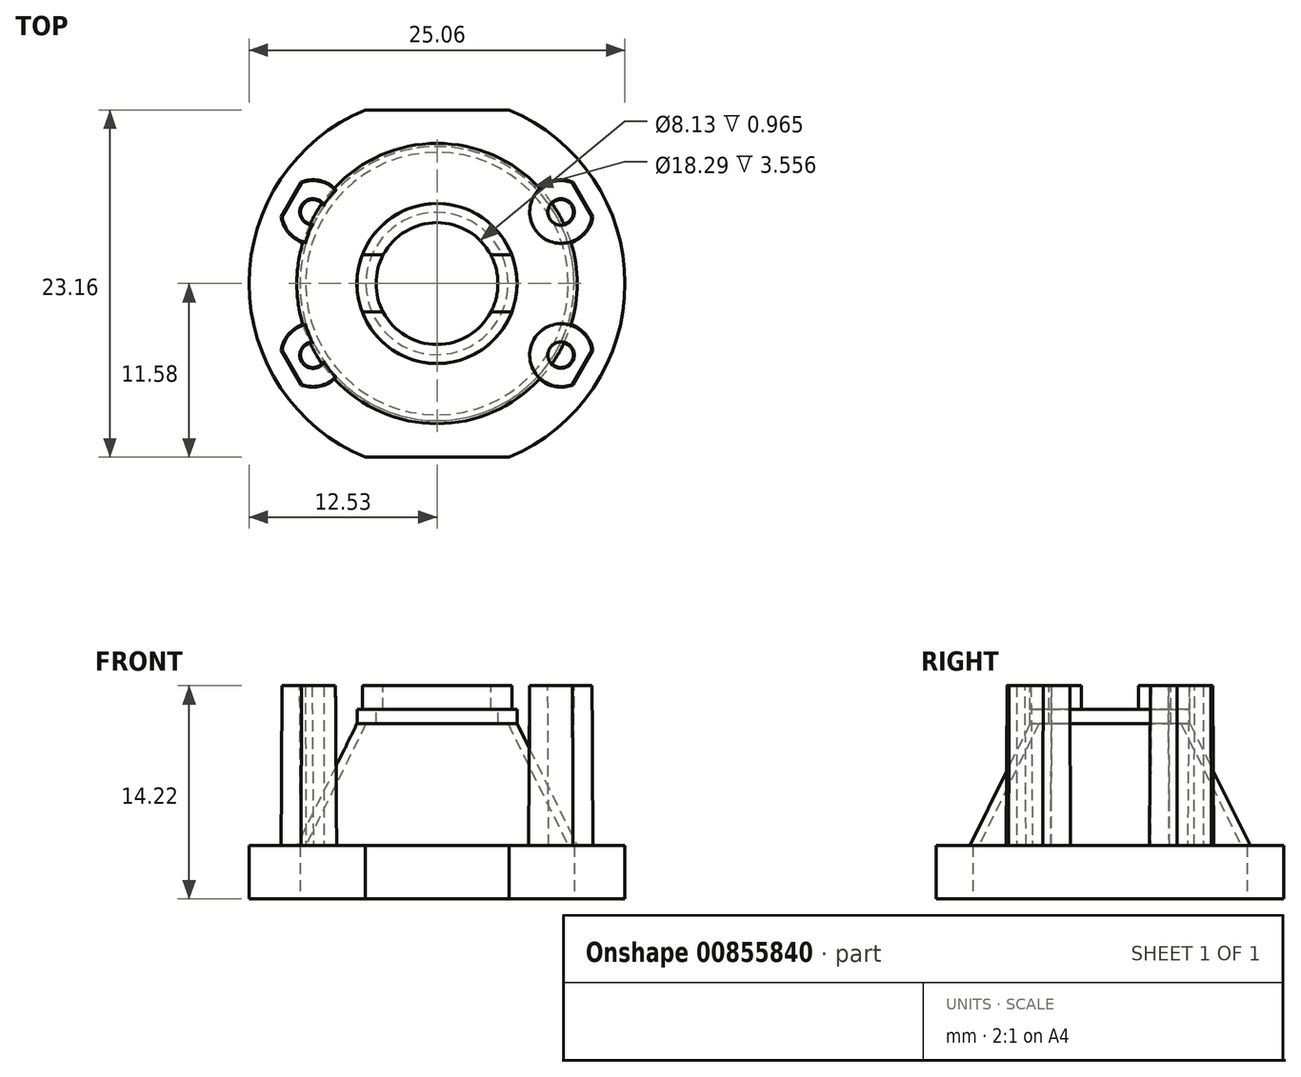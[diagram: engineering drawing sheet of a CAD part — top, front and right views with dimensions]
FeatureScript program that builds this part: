
annotation { "Feature Type Name" : "Feature", "Feature Type Description" : "" }
export const myFeature = defineFeature(function(context is Context, id is Id, definition is map)
    precondition{}
    {
        {
            var Q0;
            Q0=qCreatedBy(makeId("Top.planeOp"),FACE);
            var sketch = newSketch(context, id + "F0", { "sketchPlane" : qUnion([Q0])});
            skArc(sketch, "E0", {"start": v(-4.8, 11.58) * mm, "mid": v(-12.53, 0) * mm, "end": v(-4.8, -11.58) * mm});
            skCircle(sketch, "E1", {"center": v(0, 0) * mm, "radius": 9.14 * mm});
            skLineSegment(sketch, "E2", {"start": v(-4.8, 11.58) * mm, "end": v(4.8, 11.58) * mm});
            skLineSegment(sketch, "E3.MirrorCS", {"start": v(-4.8, -11.58) * mm, "end": v(4.8, -11.58) * mm});
            skArc(sketch, "E4.trimOffspring", {"start": v(4.8, -11.58) * mm, "mid": v(12.53, 0) * mm, "end": v(4.8, 11.58) * mm});
            skSolve(sketch);
        }
        {
            var Q0;
            Q0=makeQuery(id+"F0.imprint","IMPRINT",FACE,{"disambiguationData":[TD([[makeQuery(id+"F0.imprint","IMPRINT",EDGE,{"derivedFrom":sQuery(id+"F0.wireOp",EDGE,"E0")}),1.0]])]});
            extrude(context, id + "F1", {"entities" : qUnion([Q0]), "depth" : 3.56 * mm, "offsetDistance" : 25.4 * mm});
        }
        {
            var Q0;
            Q0=makeQuery(id+"F1.opExtrude","CAP_FACE",FACE,{"disambiguationData":[OSD([sQuery(id+"F0.wireOp",EDGE,"E0"),sQuery(id+"F0.wireOp",EDGE,"E1"),sQuery(id+"F0.wireOp",EDGE,"E2"),sQuery(id+"F0.wireOp",EDGE,"E3.MirrorCS"),sQuery(id+"F0.wireOp",EDGE,"E4.trimOffspring")])],"isStart":false});
            var sketch = newSketch(context, id + "F2", { "sketchPlane" : qUnion([Q0])});
            skCircle(sketch, "E5", {"center": v(0, 0) * mm, "radius": 9.49 * mm});
            skArc(sketch, "E6.1.0", {"start": v(-10.4, 4.47) * mm, "mid": v(-6.41, 3.7) * mm, "end": v(-9.07, 6.77) * mm});
            skLineSegment(sketch, "E6.1.1", {"start": v(-10.4, 4.47) * mm, "end": v(-9.07, 6.77) * mm});
            skArc(sketch, "E6.2.0", {"start": v(-9.07, -6.77) * mm, "mid": v(-6.41, -3.7) * mm, "end": v(-10.4, -4.47) * mm});
            skLineSegment(sketch, "E6.2.1", {"start": v(-9.07, -6.77) * mm, "end": v(-10.4, -4.47) * mm});
            skArc(sketch, "E6.4.0", {"start": v(10.4, -4.47) * mm, "mid": v(6.41, -3.7) * mm, "end": v(9.07, -6.77) * mm});
            skLineSegment(sketch, "E6.4.1", {"start": v(10.4, -4.47) * mm, "end": v(9.07, -6.77) * mm});
            skArc(sketch, "E6.5.0", {"start": v(9.07, 6.77) * mm, "mid": v(6.41, 3.7) * mm, "end": v(10.4, 4.47) * mm});
            skLineSegment(sketch, "E6.5.1", {"start": v(9.07, 6.77) * mm, "end": v(10.4, 4.47) * mm});
            skCircle(sketch, "E7", {"center": v(8.27, 4.78) * mm, "radius": 0.83 * mm});
            skCircle(sketch, "E8.MirrorC", {"center": v(8.27, -4.78) * mm, "radius": 0.83 * mm});
            skCircle(sketch, "E9.MirrorC", {"center": v(-8.27, 4.78) * mm, "radius": 0.83 * mm});
            skCircle(sketch, "E10.MirrorC", {"center": v(-8.27, -4.78) * mm, "radius": 0.83 * mm});
            skPoint(sketch, "E11", {"position": v(-9.49, 0) * mm});
            skSolve(sketch);
        }
        {
            var Q0;
            {var subQ0=sQuery(id+"F2.wireOp",EDGE,"E6.1.0");var subQ1=sQuery(id+"F2.wireOp",EDGE,"E5");var subQ2=makeQuery(id+"F2.imprint","INTERSECT",VERTEX,{"disambiguationData":[OD(0.0)],"derivedFrom":[subQ1,subQ0]});Q0=makeQuery(id+"F2.imprint","IMPRINT",FACE,{"disambiguationData":[TD([[makeQuery(id+"F2.imprint","IMPRINT",EDGE,{"disambiguationData":[TD([[subQ2,-1.0]])],"derivedFrom":subQ1}),1.0]])]});}
            var Q1;
            {var subQ0=sQuery(id+"F2.wireOp",EDGE,"E6.1.0");var subQ1=makeQuery(id+"F1.opExtrude","CAP_EDGE",EDGE,{"disambiguationData":[OSD([sQuery(id+"F0.wireOp",EDGE,"E1")])],"isStart":false});var subQ2=makeQuery(id+"F2.imprint","INTERSECT",VERTEX,{"disambiguationData":[OD(0.0)],"derivedFrom":[subQ1,subQ0]});Q1=makeQuery(id+"F2.imprint","IMPRINT",FACE,{"disambiguationData":[TD([[makeQuery(id+"F2.imprint","IMPRINT",EDGE,{"disambiguationData":[TD([[subQ2,-1.0]])],"derivedFrom":subQ0}),1.0]])]});}
            var Q2;
            {var subQ0=sQuery(id+"F2.wireOp",EDGE,"E9.MirrorC");var subQ1=sQuery(id+"F2.wireOp",EDGE,"E5");var subQ2=makeQuery(id+"F2.imprint","INTERSECT",VERTEX,{"disambiguationData":[OD(1.0)],"derivedFrom":[subQ1,subQ0]});Q2=makeQuery(id+"F2.imprint","IMPRINT",FACE,{"disambiguationData":[TD([[makeQuery(id+"F2.imprint","IMPRINT",EDGE,{"disambiguationData":[TD([[subQ2,-1.0]])],"derivedFrom":subQ1}),1.0]])]});}
            var Q3;
            {var subQ0=sQuery(id+"F2.wireOp",EDGE,"E6.1.1");Q3=makeQuery(id+"F2.imprint","IMPRINT",FACE,{"disambiguationData":[TD([[makeQuery(id+"F2.imprint","IMPRINT",EDGE,{"derivedFrom":subQ0}),-1.0]])]});}
            var Q4;
            {var subQ0=sQuery(id+"F2.wireOp",EDGE,"E6.5.0");var subQ1=makeQuery(id+"F1.opExtrude","CAP_EDGE",EDGE,{"disambiguationData":[OSD([sQuery(id+"F0.wireOp",EDGE,"E1")])],"isStart":false});var subQ2=makeQuery(id+"F2.imprint","INTERSECT",VERTEX,{"disambiguationData":[OD(0.0)],"derivedFrom":[subQ1,subQ0]});Q4=makeQuery(id+"F2.imprint","IMPRINT",FACE,{"disambiguationData":[TD([[makeQuery(id+"F2.imprint","IMPRINT",EDGE,{"disambiguationData":[TD([[subQ2,-1.0]])],"derivedFrom":subQ0}),1.0]])]});}
            var Q5;
            {var subQ0=sQuery(id+"F2.wireOp",EDGE,"E7");var subQ1=sQuery(id+"F2.wireOp",EDGE,"E5");var subQ2=makeQuery(id+"F2.imprint","INTERSECT",VERTEX,{"disambiguationData":[OD(1.0)],"derivedFrom":[subQ1,subQ0]});Q5=makeQuery(id+"F2.imprint","IMPRINT",FACE,{"disambiguationData":[TD([[makeQuery(id+"F2.imprint","IMPRINT",EDGE,{"disambiguationData":[TD([[subQ2,-1.0]])],"derivedFrom":subQ1}),1.0]])]});}
            var Q6;
            {var subQ0=sQuery(id+"F2.wireOp",EDGE,"E6.5.1");Q6=makeQuery(id+"F2.imprint","IMPRINT",FACE,{"disambiguationData":[TD([[makeQuery(id+"F2.imprint","IMPRINT",EDGE,{"derivedFrom":subQ0}),-1.0]])]});}
            var Q7;
            {var subQ0=sQuery(id+"F2.wireOp",EDGE,"E7");var subQ1=sQuery(id+"F2.wireOp",EDGE,"E5");var subQ2=makeQuery(id+"F2.imprint","INTERSECT",VERTEX,{"disambiguationData":[OD(0.0)],"derivedFrom":[subQ1,subQ0]});Q7=makeQuery(id+"F2.imprint","IMPRINT",FACE,{"disambiguationData":[TD([[makeQuery(id+"F2.imprint","IMPRINT",EDGE,{"disambiguationData":[TD([[subQ2,1.0]])],"derivedFrom":subQ1}),1.0]])]});}
            var Q8;
            {var subQ0=sQuery(id+"F2.wireOp",EDGE,"E8.MirrorC");var subQ1=sQuery(id+"F2.wireOp",EDGE,"E5");var subQ2=makeQuery(id+"F2.imprint","INTERSECT",VERTEX,{"disambiguationData":[OD(1.0)],"derivedFrom":[subQ1,subQ0]});Q8=makeQuery(id+"F2.imprint","IMPRINT",FACE,{"disambiguationData":[TD([[makeQuery(id+"F2.imprint","IMPRINT",EDGE,{"disambiguationData":[TD([[subQ2,-1.0]])],"derivedFrom":subQ1}),1.0]])]});}
            var Q9;
            {var subQ0=sQuery(id+"F2.wireOp",EDGE,"E6.4.0");var subQ1=makeQuery(id+"F1.opExtrude","CAP_EDGE",EDGE,{"disambiguationData":[OSD([sQuery(id+"F0.wireOp",EDGE,"E1")])],"isStart":false});var subQ2=makeQuery(id+"F2.imprint","INTERSECT",VERTEX,{"disambiguationData":[OD(0.0)],"derivedFrom":[subQ1,subQ0]});Q9=makeQuery(id+"F2.imprint","IMPRINT",FACE,{"disambiguationData":[TD([[makeQuery(id+"F2.imprint","IMPRINT",EDGE,{"disambiguationData":[TD([[subQ2,-1.0]])],"derivedFrom":subQ0}),1.0]])]});}
            var Q10;
            {var subQ0=sQuery(id+"F2.wireOp",EDGE,"E6.4.1");Q10=makeQuery(id+"F2.imprint","IMPRINT",FACE,{"disambiguationData":[TD([[makeQuery(id+"F2.imprint","IMPRINT",EDGE,{"derivedFrom":subQ0}),-1.0]])]});}
            var Q11;
            {var subQ0=sQuery(id+"F2.wireOp",EDGE,"E6.4.0");var subQ1=sQuery(id+"F2.wireOp",EDGE,"E5");var subQ2=makeQuery(id+"F2.imprint","INTERSECT",VERTEX,{"disambiguationData":[OD(0.0)],"derivedFrom":[subQ1,subQ0]});Q11=makeQuery(id+"F2.imprint","IMPRINT",FACE,{"disambiguationData":[TD([[makeQuery(id+"F2.imprint","IMPRINT",EDGE,{"disambiguationData":[TD([[subQ2,-1.0]])],"derivedFrom":subQ1}),1.0]])]});}
            var Q12;
            {var subQ0=sQuery(id+"F2.wireOp",EDGE,"E6.2.1");Q12=makeQuery(id+"F2.imprint","IMPRINT",FACE,{"disambiguationData":[TD([[makeQuery(id+"F2.imprint","IMPRINT",EDGE,{"derivedFrom":subQ0}),-1.0]])]});}
            var Q13;
            {var subQ0=sQuery(id+"F2.wireOp",EDGE,"E10.MirrorC");var subQ1=sQuery(id+"F2.wireOp",EDGE,"E5");var subQ2=makeQuery(id+"F2.imprint","INTERSECT",VERTEX,{"disambiguationData":[OD(1.0)],"derivedFrom":[subQ1,subQ0]});Q13=makeQuery(id+"F2.imprint","IMPRINT",FACE,{"disambiguationData":[TD([[makeQuery(id+"F2.imprint","IMPRINT",EDGE,{"disambiguationData":[TD([[subQ2,-1.0]])],"derivedFrom":subQ1}),1.0]])]});}
            var Q14;
            {var subQ0=sQuery(id+"F2.wireOp",EDGE,"E6.2.0");var subQ1=sQuery(id+"F2.wireOp",EDGE,"E5");var subQ2=makeQuery(id+"F2.imprint","INTERSECT",VERTEX,{"disambiguationData":[OD(0.0)],"derivedFrom":[subQ1,subQ0]});Q14=makeQuery(id+"F2.imprint","IMPRINT",FACE,{"disambiguationData":[TD([[makeQuery(id+"F2.imprint","IMPRINT",EDGE,{"disambiguationData":[TD([[subQ2,-1.0]])],"derivedFrom":subQ1}),1.0]])]});}
            var Q15;
            {var subQ0=sQuery(id+"F2.wireOp",EDGE,"E6.2.0");var subQ1=makeQuery(id+"F1.opExtrude","CAP_EDGE",EDGE,{"disambiguationData":[OSD([sQuery(id+"F0.wireOp",EDGE,"E1")])],"isStart":false});var subQ2=makeQuery(id+"F2.imprint","INTERSECT",VERTEX,{"disambiguationData":[OD(0.0)],"derivedFrom":[subQ1,subQ0]});Q15=makeQuery(id+"F2.imprint","IMPRINT",FACE,{"disambiguationData":[TD([[makeQuery(id+"F2.imprint","IMPRINT",EDGE,{"disambiguationData":[TD([[subQ2,-1.0]])],"derivedFrom":subQ0}),1.0]])]});}
            extrude(context, id + "F3", {"entities" : qUnion([Q0, Q1, Q2, Q3, Q4, Q5, Q6, Q7, Q8, Q9, Q10, Q11, Q12, Q13, Q14, Q15]), "operationType" : NewBodyOperationType.ADD, "depth" : 10.67 * mm, "offsetDistance" : 25.4 * mm, "hasDraft" : true, "draftAngle" : .3 * degree, "draftPullDirection" : true});
        }
        {
            var Q0;
            Q0=makeQuery(id+"F3.opExtrude","CAP_FACE",FACE,{"disambiguationData":[OSD([sQuery(id+"F2.wireOp",EDGE,"E6.1.0"),sQuery(id+"F2.wireOp",EDGE,"E6.1.1"),sQuery(id+"F2.wireOp",EDGE,"E9.MirrorC")])],"isStart":false});
            var sketch = newSketch(context, id + "F4", { "sketchPlane" : qUnion([Q0])});
            skArc(sketch, "E12", {"start": v(-4.98, -1.9) * mm, "mid": v(0, -5.33) * mm, "end": v(4.98, -1.9) * mm});
            skArc(sketch, "E13", {"start": v(-3.59, -1.9) * mm, "mid": v(0, -4.06) * mm, "end": v(3.59, -1.9) * mm});
            skLineSegment(sketch, "E14", {"start": v(3.59, 1.9) * mm, "end": v(4.98, 1.9) * mm});
            skLineSegment(sketch, "E15", {"start": v(-4.98, -1.9) * mm, "end": v(-3.59, -1.9) * mm});
            skArc(sketch, "E16.trimOffspring", {"start": v(3.59, 1.9) * mm, "mid": v(0, 4.06) * mm, "end": v(-3.59, 1.9) * mm});
            skArc(sketch, "E17.trimOffspring", {"start": v(4.98, 1.9) * mm, "mid": v(0, 5.33) * mm, "end": v(-4.98, 1.9) * mm});
            skLineSegment(sketch, "E18.trimOffspring", {"start": v(-4.98, 1.9) * mm, "end": v(-3.59, 1.9) * mm});
            skLineSegment(sketch, "E19.trimOffspring", {"start": v(3.59, -1.9) * mm, "end": v(4.98, -1.9) * mm});
            skSolve(sketch);
        }
        {
            var Q0;
            Q0 = qSketchRegion(id + "F4", true);
            extrude(context, id + "F5", {"entities" : qUnion([Q0]), "oppositeDirection" : true, "depth" : 1.57 * mm, "offsetDistance" : 25.4 * mm});
        }
        {
            var Q0;
            Q0=makeQuery(id+"F5.opExtrude","CAP_FACE",FACE,{"disambiguationData":[OSD([sQuery(id+"F4.wireOp",EDGE,"E12"),sQuery(id+"F4.wireOp",EDGE,"E13"),sQuery(id+"F4.wireOp",EDGE,"E15"),sQuery(id+"F4.wireOp",EDGE,"E19.trimOffspring")])],"isStart":false});
            var sketch = newSketch(context, id + "F6", { "sketchPlane" : qUnion([Q0])});
            skCircle(sketch, "E20", {"center": v(0, 0) * mm, "radius": 5.33 * mm});
            skPoint(sketch, "E20.first.point", {"position": v(4.62, 2.66) * mm});
            skPoint(sketch, "E20.second.point", {"position": v(-2.92, 4.46) * mm});
            skPoint(sketch, "E20.third.point", {"position": v(1.16, 5.2) * mm});
            skCircle(sketch, "E21", {"center": v(0, 0) * mm, "radius": 4.06 * mm});
            skPoint(sketch, "E21.first.point", {"position": v(3.43, 2.18) * mm});
            skPoint(sketch, "E21.second.point", {"position": v(-0.1, 4.06) * mm});
            skPoint(sketch, "E21.third.point", {"position": v(-2.86, 2.88) * mm});
            skSolve(sketch);
        }
        {
            var Q0;
            Q0 = qSketchRegion(id + "F6", true);
            extrude(context, id + "F7", {"entities" : qUnion([Q0]), "depth" : 0.97 * mm, "offsetDistance" : 25.4 * mm});
        }
        {
            var Q0;
            Q0=qCreatedBy(makeId("Right.planeOp"),FACE);
            var sketch = newSketch(context, id + "F8", { "sketchPlane" : qUnion([Q0])});
            skLineSegment(sketch, "E22", {"start": v(5.34, 11.68) * mm, "end": v(9.35, 3.56) * mm});
            skLineSegment(sketch, "E23", {"start": v(4.74, 11.68) * mm, "end": v(8.75, 3.55) * mm});
            skLineSegment(sketch, "E24", {"start": v(5.34, 11.68) * mm, "end": v(4.74, 11.68) * mm});
            skLineSegment(sketch, "E25", {"start": v(9.35, 3.56) * mm, "end": v(8.75, 3.55) * mm});
            skLineSegment(sketch, "E26", {"start": v(0, 0) * mm, "end": v(0, 3.63) * mm});
            skSolve(sketch);
        }
        {
            var Q0;
            Q0 = qSketchRegion(id + "F8", true);
            var Q1;
            Q1=sQuery(id+"F8.wireOp",EDGE,"E26");
            revolve(context, id + "F9", {"surfaceOperationType" : NewSurfaceOperationType.NEW, "entities" : qUnion([Q0]), "axis" : qUnion([Q1]), "revolveType" : RevolveType.FULL});
        }
    });
